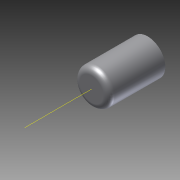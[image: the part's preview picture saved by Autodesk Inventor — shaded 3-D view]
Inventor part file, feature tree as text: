
AUTODESK INVENTOR PART (.ipt)
format: ipt  version: 2012 (Build 160160000, 160)  size: 86,016 bytes
history: native  units: in
note: dims shown in document units (in); Inventor stores cm internally (conversion verified against a paired STEP export)
features: extrude x1, fillet x1, other x1, sketch x1
ambient origin geometry x8: Origin, YZ Plane, XZ Plane, XY Plane, X Axis, Y Axis, Z Axis, Center Point
bodies: Solid1 (feature_tree)
feature tree (4):
  extrude  "Extrusion1"  Depth=0.189in TaperAngle=0.0deg
  fillet  "Fillet1"  Radius=0.0197in
  other  "Work Axis1"
  sketch  "Sketch1"  dims[d0=0.1181in d1=0.189in d2=0.0in d3=0.0197in]
